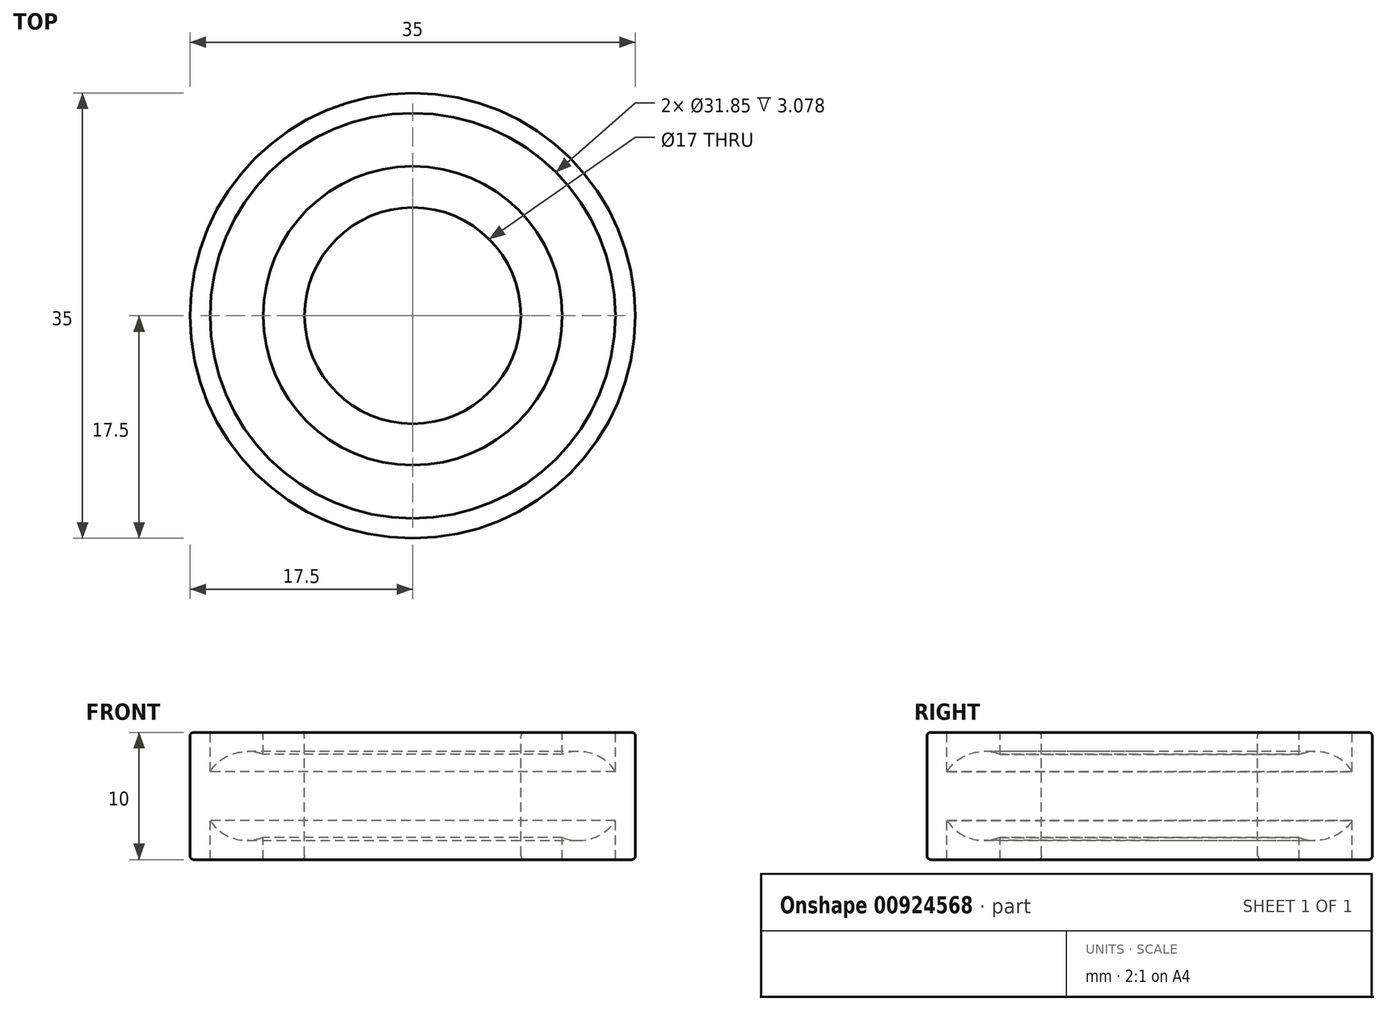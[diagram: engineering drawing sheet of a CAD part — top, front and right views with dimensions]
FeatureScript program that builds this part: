
annotation { "Feature Type Name" : "Feature", "Feature Type Description" : "" }
export const myFeature = defineFeature(function(context is Context, id is Id, definition is map)
    precondition{}
    {
        {
            assignVariable(context, id + "F0", {"name" : "r1", "anyValue" : 0.3});
        }
        {
            assignVariable(context, id + "F1", {"name" : "r2", "anyValue" : 0.3});
        }
        {
            var Q0;
            Q0=qCreatedBy(makeId("Front.planeOp"),FACE);
            var sketch = newSketch(context, id + "F2", { "sketchPlane" : qUnion([Q0])});
            skLineSegment(sketch, "E0", {"start": v(0, 10) * mm, "end": v(0, -10) * mm, "construction": true});
            skLineSegment(sketch, "E1.bottom", {"start": v(-8.5, -5) * mm, "end": v(-11.75, -5) * mm});
            skLineSegment(sketch, "E1.top", {"start": v(-8.5, 5) * mm, "end": v(-11.75, 5) * mm});
            skLineSegment(sketch, "E1.left", {"start": v(-8.5, -5) * mm, "end": v(-8.5, 5) * mm});
            skLineSegment(sketch, "E1.right", {"start": v(-17.5, -5) * mm, "end": v(-17.5, 5) * mm});
            skPoint(sketch, "E1.middle", {"position": v(-13, 0) * mm});
            skArc(sketch, "E2", {"start": v(-15.93, -1.92) * mm, "mid": v(-14.07, -3.33) * mm, "end": v(-11.75, -3.27) * mm});
            skLineSegment(sketch, "E3", {"start": v(-11.75, 5) * mm, "end": v(-11.75, 3.27) * mm});
            skLineSegment(sketch, "E4", {"start": v(-15.93, 5) * mm, "end": v(-15.93, 1.92) * mm});
            skLineSegment(sketch, "E5.trimOffspring", {"start": v(-15.93, 5) * mm, "end": v(-17.5, 5) * mm});
            skLineSegment(sketch, "E6.trimOffspring", {"start": v(-15.93, -1.92) * mm, "end": v(-15.93, -5) * mm});
            skLineSegment(sketch, "E7.trimOffspring", {"start": v(-11.75, -3.27) * mm, "end": v(-11.75, -5) * mm});
            skArc(sketch, "E8.trimOffspring", {"start": v(-11.75, 3.27) * mm, "mid": v(-14.07, 3.33) * mm, "end": v(-15.93, 1.92) * mm});
            skLineSegment(sketch, "E9.trimOffspring", {"start": v(-15.93, -5) * mm, "end": v(-17.5, -5) * mm});
            skSolve(sketch);
        }
        {
            var Q0;
            Q0=makeQuery(id+"F2.imprint","IMPRINT",FACE,{"disambiguationData":[TD([[makeQuery(id+"F2.imprint","IMPRINT",EDGE,{"derivedFrom":sQuery(id+"F2.wireOp",EDGE,"E1.bottom")}),-1.0]])]});
            var Q1;
            Q1=sQuery(id+"F2.wireOp",EDGE,"E0");
            revolve(context, id + "F3", {"surfaceOperationType" : NewSurfaceOperationType.NEW, "entities" : qUnion([Q0]), "axis" : qUnion([Q1]), "revolveType" : RevolveType.FULL});
        }
        {
            var Q0;
            Q0=makeQuery(id+"F3.opRevolve","SWEPT_EDGE",EDGE,{"disambiguationData":[OSD([sQuery(id+"F2.wireOp",EDGE,"E1.right"),sQuery(id+"F2.wireOp",EDGE,"E5.trimOffspring")])]});
            var Q1;
            Q1=makeQuery(id+"F3.opRevolve","SWEPT_EDGE",EDGE,{"disambiguationData":[OSD([sQuery(id+"F2.wireOp",EDGE,"E1.right"),sQuery(id+"F2.wireOp",EDGE,"E9.trimOffspring")])]});
            fillet(context, id + "F4", {"entities" : qUnion([Q0, Q1]), "radius" : (getVariable(context, 'r1')) * mm, "tangentPropagation" : true, "allowEdgeOverflow" : false});
        }
        {
            var Q0;
            Q0=makeQuery(id+"F3.opRevolve","SWEPT_EDGE",EDGE,{"disambiguationData":[OSD([sQuery(id+"F2.wireOp",EDGE,"E1.top"),sQuery(id+"F2.wireOp",EDGE,"E1.left")])]});
            var Q1;
            Q1=makeQuery(id+"F3.opRevolve","SWEPT_EDGE",EDGE,{"disambiguationData":[OSD([sQuery(id+"F2.wireOp",EDGE,"E1.bottom"),sQuery(id+"F2.wireOp",EDGE,"E1.left")])]});
            fillet(context, id + "F5", {"entities" : qUnion([Q0, Q1]), "radius" : (getVariable(context, 'r2')) * mm, "tangentPropagation" : true, "allowEdgeOverflow" : false});
        }
    });
